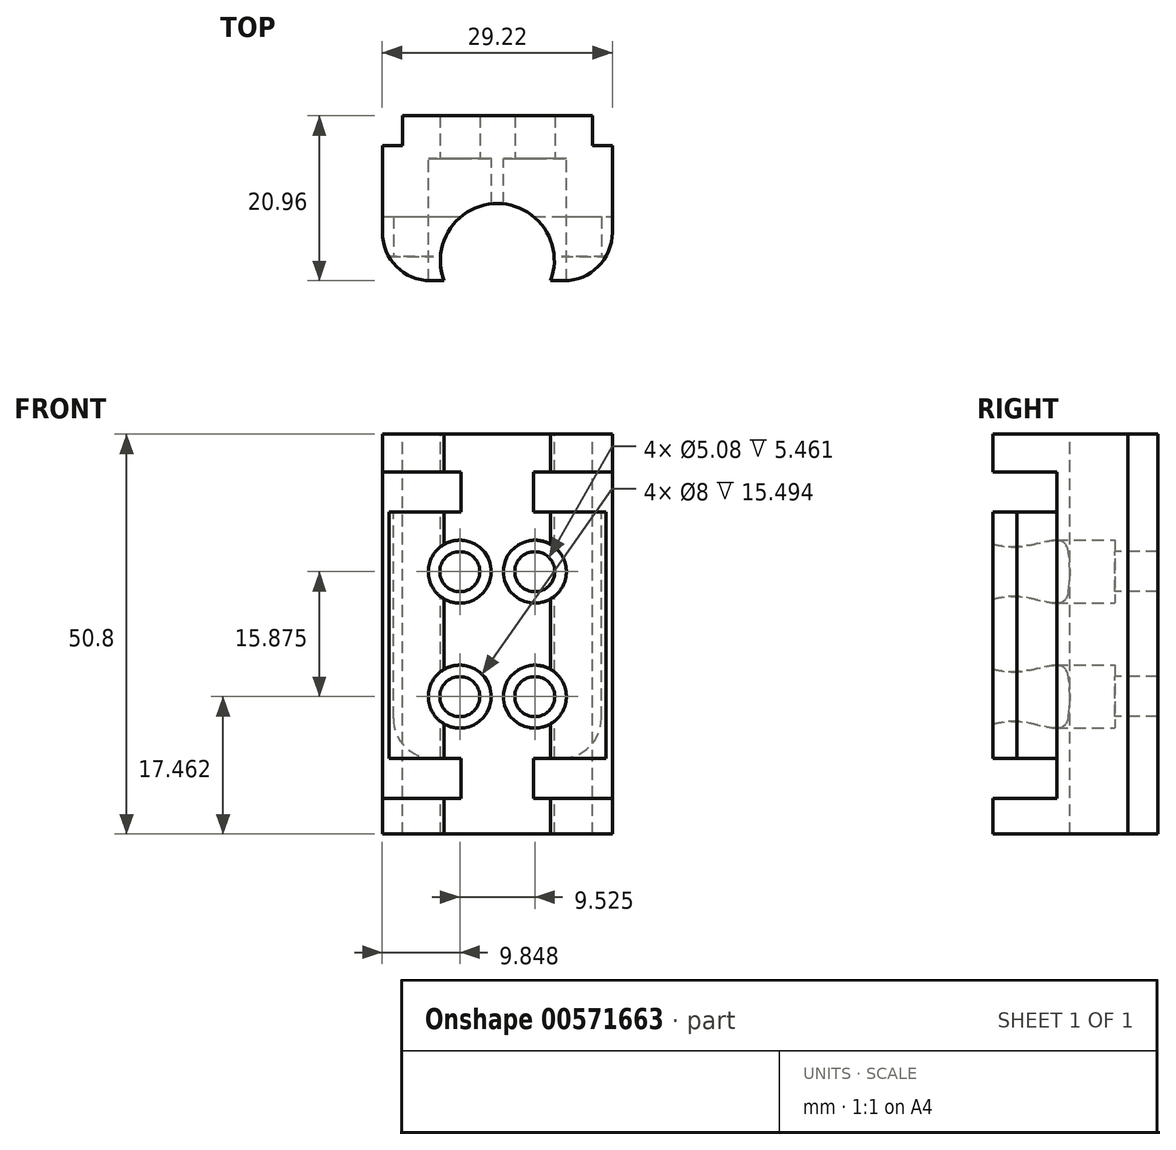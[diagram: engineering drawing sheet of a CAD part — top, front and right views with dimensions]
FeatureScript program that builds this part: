
annotation { "Feature Type Name" : "Feature", "Feature Type Description" : "" }
export const myFeature = defineFeature(function(context is Context, id is Id, definition is map)
    precondition{}
    {
        {
            var Q0;
            Q0=qCreatedBy(makeId("Front.planeOp"),FACE);
            var sketch = newSketch(context, id + "F0", { "sketchPlane" : qUnion([Q0])});
            skLineSegment(sketch, "E0.bottom", {"start": v(14.6, -25.4) * mm, "end": v(-14.6, -25.4) * mm});
            skLineSegment(sketch, "E0.top", {"start": v(14.6, 25.4) * mm, "end": v(-14.6, 25.4) * mm});
            skLineSegment(sketch, "E0.left", {"start": v(14.6, -25.4) * mm, "end": v(14.6, 25.4) * mm});
            skLineSegment(sketch, "E0.right", {"start": v(-14.6, -25.4) * mm, "end": v(-14.6, 25.4) * mm});
            skPoint(sketch, "E0.middle", {"position": v(0, 0) * mm});
            skSolve(sketch);
        }
        {
            var Q0;
            Q0=makeQuery(id+"F0.imprint","IMPRINT",FACE,{"disambiguationData":[TD([[makeQuery(id+"F0.imprint","IMPRINT",EDGE,{"derivedFrom":sQuery(id+"F0.wireOp",EDGE,"E0.bottom")}),-1.0]])]});
            extrude(context, id + "F1", {"entities" : qUnion([Q0]), "depth" : 1.65 * mm, "offsetDistance" : 25.4 * mm});
        }
        {
            var Q0;
            Q0=makeQuery(id+"F1.opExtrude","CAP_FACE",FACE,{"disambiguationData":[OSD([sQuery(id+"F0.wireOp",EDGE,"E0.bottom"),sQuery(id+"F0.wireOp",EDGE,"E0.top"),sQuery(id+"F0.wireOp",EDGE,"E0.left"),sQuery(id+"F0.wireOp",EDGE,"E0.right")])],"isStart":false});
            var sketch = newSketch(context, id + "F2", { "sketchPlane" : qUnion([Q0])});
            skPoint(sketch, "E1.middle", {"position": v(0, 0) * mm});
            skCircle(sketch, "E2", {"center": v(-4.76, 7.94) * mm, "radius": 2.54 * mm});
            skCircle(sketch, "E3", {"center": v(4.76, 7.94) * mm, "radius": 2.54 * mm});
            skCircle(sketch, "E4", {"center": v(-4.76, -7.94) * mm, "radius": 2.54 * mm});
            skCircle(sketch, "E5", {"center": v(4.76, -7.94) * mm, "radius": 2.54 * mm});
            skSolve(sketch);
        }
        {
            var Q0;
            Q0 = qSketchRegion(id + "F2", true);
            extrude(context, id + "F3", {"entities" : qUnion([Q0]), "operationType" : NewBodyOperationType.REMOVE, "oppositeDirection" : true, "depth" : 25.4 * mm, "offsetDistance" : 25.4 * mm});
        }
        {
            var Q0;
            Q0=makeQuery(id+"F1.opExtrude","CAP_FACE",FACE,{"disambiguationData":[OSD([sQuery(id+"F0.wireOp",EDGE,"E0.bottom"),sQuery(id+"F0.wireOp",EDGE,"E0.top"),sQuery(id+"F0.wireOp",EDGE,"E0.left"),sQuery(id+"F0.wireOp",EDGE,"E0.right")])],"isStart":false});
            var sketch = newSketch(context, id + "F4", { "sketchPlane" : qUnion([Q0])});
            skLineSegment(sketch, "E6.bottom", {"start": v(14.6, -25.4) * mm, "end": v(-14.6, -25.4) * mm});
            skLineSegment(sketch, "E6.top", {"start": v(14.6, 25.4) * mm, "end": v(-14.6, 25.4) * mm});
            skLineSegment(sketch, "E6.left", {"start": v(14.6, -25.4) * mm, "end": v(14.6, 25.4) * mm});
            skLineSegment(sketch, "E6.right", {"start": v(-14.6, -25.4) * mm, "end": v(-14.6, 25.4) * mm});
            skPoint(sketch, "E6.middle", {"position": v(0, 0) * mm});
            skSolve(sketch);
        }
        {
            var Q0;
            Q0 = qSketchRegion(id + "F4", true);
            extrude(context, id + "F5", {"entities" : qUnion([Q0]), "operationType" : NewBodyOperationType.ADD, "depth" : 5.33 * mm, "offsetDistance" : 25.4 * mm});
        }
        {
            var Q0;
            Q0=makeQuery(id+"F5.boolean.opBoolean","SPLIT",FACE,{"disambiguationData":[TD([makeQuery(id+"F3.boolean.opBoolean","COPY",FACE,{"derivedFrom":makeQuery(id+"F3.opExtrude","SWEPT_FACE",FACE,{"disambiguationData":[OSD([sQuery(id+"F2.wireOp",EDGE,"E3")])]})})])],"derivedFrom":makeQuery(id+"F5.opExtrude","CAP_FACE",FACE,{"disambiguationData":[OSD([sQuery(id+"F4.wireOp",EDGE,"E6.bottom"),sQuery(id+"F4.wireOp",EDGE,"E6.top"),sQuery(id+"F4.wireOp",EDGE,"E6.left"),sQuery(id+"F4.wireOp",EDGE,"E6.right")])],"isStart":true})});
            var sketch = newSketch(context, id + "F6", { "sketchPlane" : qUnion([Q0])});
            skCircle(sketch, "E7", {"center": v(-4.76, 7.94) * mm, "radius": 4 * mm});
            skPoint(sketch, "E8.middle", {"position": v(0, 0) * mm});
            skCircle(sketch, "E9", {"center": v(4.76, 7.94) * mm, "radius": 4 * mm});
            skCircle(sketch, "E10", {"center": v(-4.76, -7.94) * mm, "radius": 4 * mm});
            skCircle(sketch, "E11", {"center": v(4.76, -7.94) * mm, "radius": 4 * mm});
            skSolve(sketch);
        }
        {
            var Q0;
            Q0 = qSketchRegion(id + "F6", true);
            extrude(context, id + "F7", {"entities" : qUnion([Q0]), "operationType" : NewBodyOperationType.REMOVE, "oppositeDirection" : true, "depth" : 53.85 * mm, "offsetDistance" : 25.4 * mm});
        }
        {
            var Q0;
            Q0=makeQuery(id+"F5.opExtrude","CAP_FACE",FACE,{"disambiguationData":[OSD([sQuery(id+"F4.wireOp",EDGE,"E6.bottom"),sQuery(id+"F4.wireOp",EDGE,"E6.top"),sQuery(id+"F4.wireOp",EDGE,"E6.left"),sQuery(id+"F4.wireOp",EDGE,"E6.right")])],"isStart":false});
            var sketch = newSketch(context, id + "F8", { "sketchPlane" : qUnion([Q0])});
            skLineSegment(sketch, "E12.bottom", {"start": v(14.6, -25.4) * mm, "end": v(-14.6, -25.4) * mm});
            skLineSegment(sketch, "E12.top", {"start": v(14.6, 25.4) * mm, "end": v(-14.6, 25.4) * mm});
            skLineSegment(sketch, "E12.left", {"start": v(14.6, -25.4) * mm, "end": v(14.6, 25.4) * mm});
            skLineSegment(sketch, "E12.right", {"start": v(-14.6, -25.4) * mm, "end": v(-14.6, 25.4) * mm});
            skPoint(sketch, "E12.middle", {"position": v(0, 0) * mm});
            skSolve(sketch);
        }
        {
            var Q0;
            Q0=makeQuery(id+"F8.imprint","IMPRINT",FACE,{"disambiguationData":[TD([[makeQuery(id+"F8.imprint","IMPRINT",EDGE,{"derivedFrom":sQuery(id+"F8.wireOp",EDGE,"E12.bottom")}),-1.0]])]});
            extrude(context, id + "F9", {"entities" : qUnion([Q0]), "operationType" : NewBodyOperationType.ADD, "depth" : 10.16 * mm, "offsetDistance" : 25.4 * mm});
        }
        {
            var Q0;
            Q0=makeQuery(id+"F9.boolean.opBoolean","MERGE",FACE,{"derivedFrom":[makeQuery(id+"F5.boolean.opBoolean","MERGE",FACE,{"derivedFrom":[makeQuery(id+"F1.opExtrude","SWEPT_FACE",FACE,{"disambiguationData":[OSD([sQuery(id+"F0.wireOp",EDGE,"E0.top")])]}),makeQuery(id+"F5.opExtrude","SWEPT_FACE",FACE,{"disambiguationData":[OSD([sQuery(id+"F4.wireOp",EDGE,"E6.top")])]})]}),makeQuery(id+"F9.opExtrude","SWEPT_FACE",FACE,{"disambiguationData":[OSD([sQuery(id+"F8.wireOp",EDGE,"E12.top")])]})]});
            var sketch = newSketch(context, id + "F10", { "sketchPlane" : qUnion([Q0])});
            skCircle(sketch, "E13", {"center": v(0, -14.59) * mm, "radius": 7.24 * mm});
            skSolve(sketch);
        }
        {
            var Q0;
            Q0=makeQuery(id+"F10.imprint","IMPRINT",FACE,{"disambiguationData":[TD([[makeQuery(id+"F10.imprint","IMPRINT",EDGE,{"derivedFrom":sQuery(id+"F10.wireOp",EDGE,"E13")}),1.0]])]});
            extrude(context, id + "F11", {"entities" : qUnion([Q0]), "operationType" : NewBodyOperationType.REMOVE, "oppositeDirection" : true, "depth" : 54.6 * mm, "offsetDistance" : 25.4 * mm});
        }
        {
            var Q0;
            Q0=makeQuery(id+"F9.opExtrude","CAP_EDGE",EDGE,{"disambiguationData":[OSD([sQuery(id+"F8.wireOp",EDGE,"E12.left")])],"isStart":false});
            var Q1;
            Q1=makeQuery(id+"F9.opExtrude","CAP_EDGE",EDGE,{"disambiguationData":[OSD([sQuery(id+"F8.wireOp",EDGE,"E12.right")])],"isStart":false});
            fillet(context, id + "F12", {"entities" : qUnion([Q0, Q1]), "radius" : 6.13 * mm, "tangentPropagation" : true, "allowEdgeOverflow" : false});
        }
        {
            var Q0;
            {var subQ0=sQuery(id+"F8.wireOp",EDGE,"E12.top");var subQ1=sQuery(id+"F6.wireOp",EDGE,"E11");var subQ2=sQuery(id+"F4.wireOp",EDGE,"E6.right");var subQ3=sQuery(id+"F4.wireOp",EDGE,"E6.top");var subQ4=sQuery(id+"F8.wireOp",EDGE,"E12.bottom");var subQ5=sQuery(id+"F6.wireOp",EDGE,"E9");var subQ6=sQuery(id+"F4.wireOp",EDGE,"E6.bottom");var subQ7=sQuery(id+"F8.wireOp",EDGE,"E12.right");var subQ8=sQuery(id+"F4.wireOp",EDGE,"E6.left");Q0=makeQuery(id+"F12.opFillet","SPLIT",FACE,{"disambiguationData":[OD(0.0)],"derivedFrom":makeQuery(id+"F11.boolean.opBoolean","SPLIT",FACE,{"disambiguationData":[TD([makeQuery(id+"F1.opExtrude","SWEPT_FACE",FACE,{"disambiguationData":[OSD([sQuery(id+"F0.wireOp",EDGE,"E0.right")])]})])],"derivedFrom":makeQuery(id+"F9.opExtrude","CAP_FACE",FACE,{"disambiguationData":[OSD([subQ6,subQ3,subQ8,subQ2,sQuery(id+"F6.wireOp",EDGE,"E7"),subQ5,sQuery(id+"F6.wireOp",EDGE,"E10"),subQ1,subQ4,subQ0,sQuery(id+"F8.wireOp",EDGE,"E12.left"),subQ7])],"isStart":false})})});}
            var sketch = newSketch(context, id + "F13", { "sketchPlane" : qUnion([Q0])});
            skLineSegment(sketch, "E14.bottom", {"start": v(-21.8, 20.6) * mm, "end": v(21.8, 20.6) * mm});
            skLineSegment(sketch, "E14.top", {"start": v(-21.8, 15.51) * mm, "end": v(21.8, 15.51) * mm});
            skLineSegment(sketch, "E14.left", {"start": v(-21.8, 20.6) * mm, "end": v(-21.8, 15.51) * mm});
            skLineSegment(sketch, "E14.right", {"start": v(21.8, 20.6) * mm, "end": v(21.8, 15.51) * mm});
            skPoint(sketch, "E14.middle", {"position": v(0, 18.05) * mm});
            skLineSegment(sketch, "E15.bottom", {"start": v(-21.8, -15.78) * mm, "end": v(21.8, -15.78) * mm});
            skLineSegment(sketch, "E15.top", {"start": v(-21.8, -20.86) * mm, "end": v(21.8, -20.86) * mm});
            skLineSegment(sketch, "E15.left", {"start": v(-21.8, -15.78) * mm, "end": v(-21.8, -20.86) * mm});
            skLineSegment(sketch, "E15.right", {"start": v(21.8, -15.78) * mm, "end": v(21.8, -20.86) * mm});
            skPoint(sketch, "E15.middle", {"position": v(0, -18.32) * mm});
            skSolve(sketch);
        }
        {
            var Q0;
            Q0 = qSketchRegion(id + "F13", true);
            extrude(context, id + "F14", {"entities" : qUnion([Q0]), "operationType" : NewBodyOperationType.REMOVE, "oppositeDirection" : true, "depth" : 8.13 * mm, "offsetDistance" : 25.4 * mm});
        }
        {
            var Q0;
            Q0=makeQuery(id+"F9.boolean.opBoolean","MERGE",FACE,{"derivedFrom":[makeQuery(id+"F5.boolean.opBoolean","MERGE",FACE,{"derivedFrom":[makeQuery(id+"F1.opExtrude","SWEPT_FACE",FACE,{"disambiguationData":[OSD([sQuery(id+"F0.wireOp",EDGE,"E0.right")])]}),makeQuery(id+"F5.opExtrude","SWEPT_FACE",FACE,{"disambiguationData":[OSD([sQuery(id+"F4.wireOp",EDGE,"E6.right")])]})]}),makeQuery(id+"F9.opExtrude","SWEPT_FACE",FACE,{"disambiguationData":[OSD([sQuery(id+"F8.wireOp",EDGE,"E12.right")])]})]});
            var sketch = newSketch(context, id + "F15", { "sketchPlane" : qUnion([Q0])});
            skLineSegment(sketch, "E16.bottom", {"start": v(9.02, 15.51) * mm, "end": v(14.1, 15.51) * mm});
            skLineSegment(sketch, "E16.top", {"start": v(9.02, -16.24) * mm, "end": v(14.1, -16.24) * mm});
            skLineSegment(sketch, "E16.left", {"start": v(9.02, 15.51) * mm, "end": v(9.02, -16.24) * mm});
            skLineSegment(sketch, "E16.right", {"start": v(14.1, 15.51) * mm, "end": v(14.1, -16.24) * mm});
            skSolve(sketch);
        }
        {
            var Q0;
            Q0 = qSketchRegion(id + "F15", true);
            extrude(context, id + "F16", {"entities" : qUnion([Q0]), "operationType" : NewBodyOperationType.REMOVE, "oppositeDirection" : true, "depth" : 1.4 * mm, "offsetDistance" : 25.4 * mm});
        }
        {
            var Q0;
            Q0=makeQuery(id+"F9.boolean.opBoolean","MERGE",FACE,{"derivedFrom":[makeQuery(id+"F5.boolean.opBoolean","MERGE",FACE,{"derivedFrom":[makeQuery(id+"F1.opExtrude","SWEPT_FACE",FACE,{"disambiguationData":[OSD([sQuery(id+"F0.wireOp",EDGE,"E0.left")])]}),makeQuery(id+"F5.opExtrude","SWEPT_FACE",FACE,{"disambiguationData":[OSD([sQuery(id+"F4.wireOp",EDGE,"E6.left")])]})]}),makeQuery(id+"F9.opExtrude","SWEPT_FACE",FACE,{"disambiguationData":[OSD([sQuery(id+"F8.wireOp",EDGE,"E12.left")])]})]});
            var sketch = newSketch(context, id + "F17", { "sketchPlane" : qUnion([Q0])});
            skLineSegment(sketch, "E17.bottom", {"start": v(-9.02, 15.51) * mm, "end": v(-14.09, 15.51) * mm});
            skLineSegment(sketch, "E17.top", {"start": v(-9.02, -15.93) * mm, "end": v(-14.09, -15.93) * mm});
            skLineSegment(sketch, "E17.left", {"start": v(-9.02, 15.51) * mm, "end": v(-9.02, -15.93) * mm});
            skLineSegment(sketch, "E17.right", {"start": v(-14.09, 15.51) * mm, "end": v(-14.09, -15.93) * mm});
            skSolve(sketch);
        }
        {
            var Q0;
            Q0 = qSketchRegion(id + "F17", true);
            extrude(context, id + "F18", {"entities" : qUnion([Q0]), "operationType" : NewBodyOperationType.REMOVE, "oppositeDirection" : true, "depth" : 1.4 * mm, "offsetDistance" : 25.4 * mm});
        }
        {
            var Q0;
            Q0=makeQuery(id+"F18.boolean.opBoolean","COPY",EDGE,{"derivedFrom":makeQuery(id+"F18.opExtrude","CAP_EDGE",EDGE,{"disambiguationData":[OSD([sQuery(id+"F17.wireOp",EDGE,"E17.bottom")])],"isStart":false})});
            var Q1;
            Q1=makeQuery(id+"F16.boolean.opBoolean","COPY",EDGE,{"derivedFrom":makeQuery(id+"F16.opExtrude","CAP_EDGE",EDGE,{"disambiguationData":[OSD([sQuery(id+"F15.wireOp",EDGE,"E16.bottom")])],"isStart":false})});
            var Q2;
            {var subQ2=sQuery(id+"F13.wireOp",EDGE,"E15.bottom");Q2=makeQuery(id+"F16.boolean.opBoolean","INTERSECT",EDGE,{"derivedFrom":[makeQuery(id+"F14.boolean.opBoolean","COPY",FACE,{"disambiguationData":[TD([makeQuery(id+"F1.opExtrude","SWEPT_FACE",FACE,{"disambiguationData":[OSD([sQuery(id+"F0.wireOp",EDGE,"E0.right")])]})])],"derivedFrom":makeQuery(id+"F14.opExtrude","SWEPT_FACE",FACE,{"disambiguationData":[OSD([subQ2])]})}),makeQuery(id+"F16.opExtrude","CAP_FACE",FACE,{"disambiguationData":[OSD([sQuery(id+"F15.wireOp",EDGE,"E16.bottom"),sQuery(id+"F15.wireOp",EDGE,"E16.top"),sQuery(id+"F15.wireOp",EDGE,"E16.left"),sQuery(id+"F15.wireOp",EDGE,"E16.right")])],"isStart":false})]});}
            var Q3;
            {var subQ2=sQuery(id+"F13.wireOp",EDGE,"E15.bottom");Q3=makeQuery(id+"F18.boolean.opBoolean","INTERSECT",EDGE,{"derivedFrom":[makeQuery(id+"F14.boolean.opBoolean","COPY",FACE,{"disambiguationData":[TD([makeQuery(id+"F1.opExtrude","SWEPT_FACE",FACE,{"disambiguationData":[OSD([sQuery(id+"F0.wireOp",EDGE,"E0.left")])]})])],"derivedFrom":makeQuery(id+"F14.opExtrude","SWEPT_FACE",FACE,{"disambiguationData":[OSD([subQ2])]})}),makeQuery(id+"F18.opExtrude","CAP_FACE",FACE,{"disambiguationData":[OSD([sQuery(id+"F17.wireOp",EDGE,"E17.bottom"),sQuery(id+"F17.wireOp",EDGE,"E17.top"),sQuery(id+"F17.wireOp",EDGE,"E17.left"),sQuery(id+"F17.wireOp",EDGE,"E17.right")])],"isStart":false})]});}
            fillet(context, id + "F19", {"entities" : qUnion([Q0, Q1, Q2, Q3]), "radius" : 5.08 * mm, "tangentPropagation" : true, "allowEdgeOverflow" : false});
        }
        {
            var Q0;
            Q0=makeQuery(id+"F1.opExtrude","CAP_FACE",FACE,{"disambiguationData":[OSD([sQuery(id+"F0.wireOp",EDGE,"E0.bottom"),sQuery(id+"F0.wireOp",EDGE,"E0.top"),sQuery(id+"F0.wireOp",EDGE,"E0.left"),sQuery(id+"F0.wireOp",EDGE,"E0.right")])],"isStart":true});
            var sketch = newSketch(context, id + "F20", { "sketchPlane" : qUnion([Q0])});
            skLineSegment(sketch, "E18.bottom", {"start": v(-12.07, -25.4) * mm, "end": v(12.07, -25.4) * mm});
            skLineSegment(sketch, "E18.top", {"start": v(-12.07, 25.4) * mm, "end": v(12.07, 25.4) * mm});
            skLineSegment(sketch, "E18.left", {"start": v(-12.07, -25.4) * mm, "end": v(-12.07, 25.4) * mm});
            skLineSegment(sketch, "E18.right", {"start": v(12.07, -25.4) * mm, "end": v(12.07, 25.4) * mm});
            skPoint(sketch, "E18.middle", {"position": v(0, 0) * mm});
            skSolve(sketch);
        }
        {
            var Q0;
            Q0=makeQuery(id+"F20.imprint","IMPRINT",FACE,{"disambiguationData":[TD([[makeQuery(id+"F20.imprint","IMPRINT",EDGE,{"derivedFrom":sQuery(id+"F20.wireOp",EDGE,"E18.bottom")}),1.0]])]});
            extrude(context, id + "F21", {"entities" : qUnion([Q0]), "operationType" : NewBodyOperationType.ADD, "depth" : 3.8 * mm, "offsetDistance" : 25.4 * mm});
        }
    });
